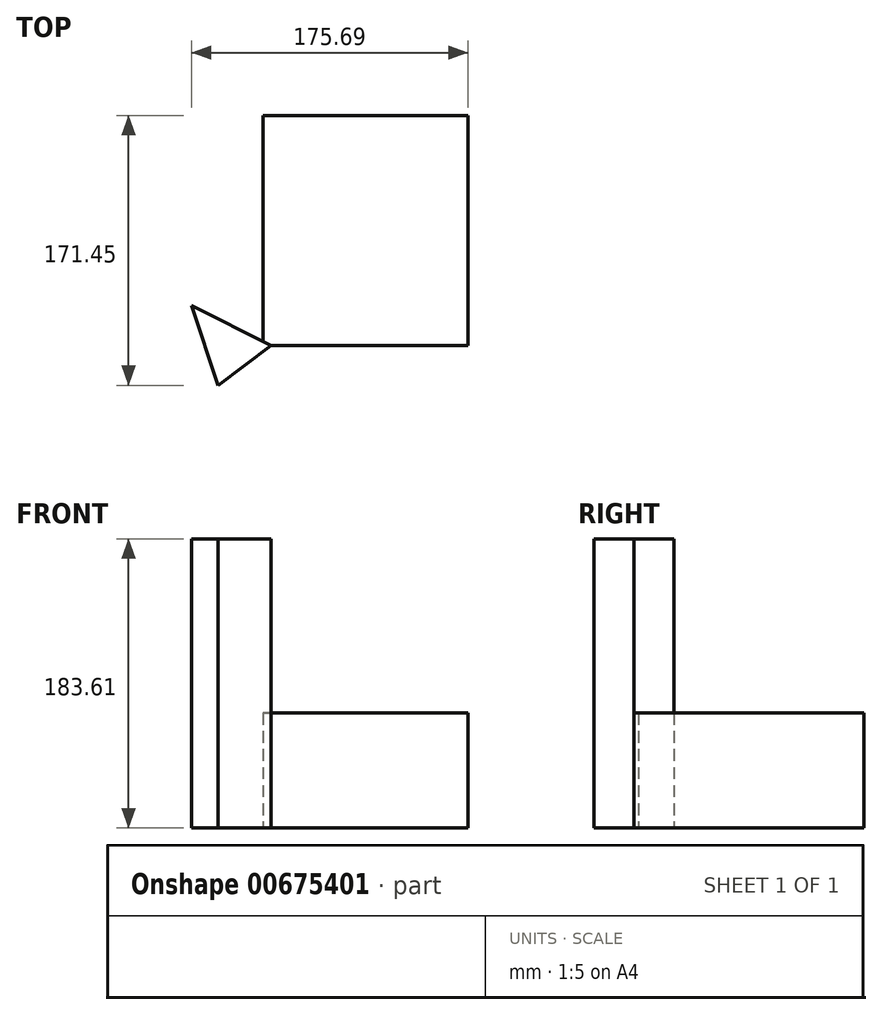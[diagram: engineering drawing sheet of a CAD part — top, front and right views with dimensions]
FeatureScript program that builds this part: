
annotation { "Feature Type Name" : "Feature", "Feature Type Description" : "" }
export const myFeature = defineFeature(function(context is Context, id is Id, definition is map)
    precondition{}
    {
        {
            var Q0;
            Q0=qCreatedBy(makeId("Top.planeOp"),FACE);
            var sketch = newSketch(context, id + "F0", { "sketchPlane" : qUnion([Q0])});
            skLineSegment(sketch, "E0.bottom", {"start": v(0, 0) * mm, "end": v(130.33, 0) * mm});
            skLineSegment(sketch, "E0.top", {"start": v(0, 146) * mm, "end": v(130.33, 146) * mm});
            skLineSegment(sketch, "E0.left", {"start": v(0, 0) * mm, "end": v(0, 146) * mm});
            skLineSegment(sketch, "E0.right", {"start": v(130.33, 0) * mm, "end": v(130.33, 146) * mm});
            skSolve(sketch);
        }
        {
            var Q0;
            Q0=makeQuery(id+"F0.imprint","IMPRINT",FACE,{"disambiguationData":[TD([[makeQuery(id+"F0.imprint","IMPRINT",EDGE,{"derivedFrom":sQuery(id+"F0.wireOp",EDGE,"E0.bottom")}),1.0]])]});
            extrude(context, id + "F1", {"entities" : qUnion([Q0]), "depth" : 73.11 * mm, "offsetDistance" : 25.4 * mm});
        }
        {
            var Q0;
            Q0=qCreatedBy(makeId("Top.planeOp"),FACE);
            var sketch = newSketch(context, id + "F2", { "sketchPlane" : qUnion([Q0])});
            skLineSegment(sketch, "E1", {"start": v(-45.36, 25.42) * mm, "end": v(5.23, 0.02) * mm});
            skLineSegment(sketch, "E2", {"start": v(5.23, 0.02) * mm, "end": v(-28.41, -25.45) * mm});
            skLineSegment(sketch, "E3", {"start": v(-28.41, -25.45) * mm, "end": v(-45.36, 25.42) * mm});
            skSolve(sketch);
        }
        {
            var Q0;
            Q0=makeQuery(id+"F2.imprint","IMPRINT",FACE,{"disambiguationData":[TD([[makeQuery(id+"F2.imprint","IMPRINT",EDGE,{"derivedFrom":sQuery(id+"F2.wireOp",EDGE,"E1")}),-1.0]])]});
            extrude(context, id + "F3", {"entities" : qUnion([Q0]), "operationType" : NewBodyOperationType.ADD, "depth" : 183.61 * mm, "offsetDistance" : 25.4 * mm});
        }
    });
